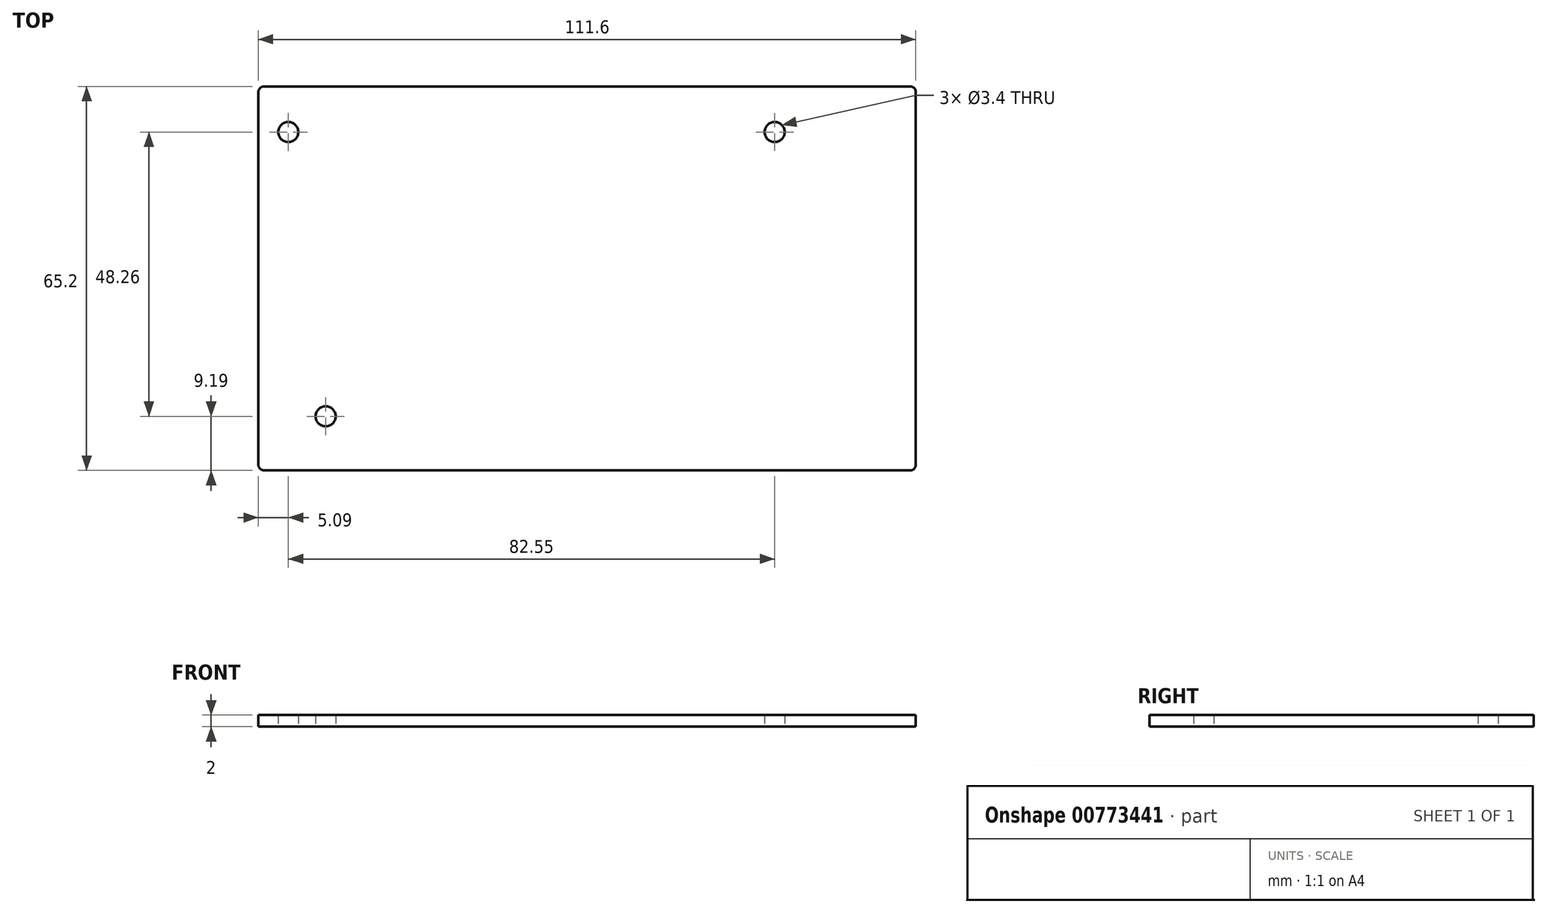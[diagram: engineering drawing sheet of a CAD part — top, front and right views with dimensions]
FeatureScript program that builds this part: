
annotation { "Feature Type Name" : "Feature", "Feature Type Description" : "" }
export const myFeature = defineFeature(function(context is Context, id is Id, definition is map)
    precondition{}
    {
        {
            var Q0;
            Q0=qCreatedBy(makeId("Top.planeOp"),FACE);
            var sketch = newSketch(context, id + "F0", { "sketchPlane" : qUnion([Q0])});
            skLineSegment(sketch, "E0.bottom", {"start": v(54.8, -32.6) * mm, "end": v(-54.8, -32.6) * mm});
            skLineSegment(sketch, "E0.top", {"start": v(54.8, 32.6) * mm, "end": v(-54.8, 32.6) * mm});
            skLineSegment(sketch, "E0.left", {"start": v(55.8, -31.6) * mm, "end": v(55.8, 31.6) * mm});
            skLineSegment(sketch, "E0.right", {"start": v(-55.8, -31.6) * mm, "end": v(-55.8, 31.6) * mm});
            skPoint(sketch, "E0.middle", {"position": v(0, 0) * mm});
            skLineSegment(sketch, "E1", {"start": v(-55.8, -32.6) * mm, "end": v(-55.8, -23.41) * mm, "construction": true});
            skLineSegment(sketch, "E2", {"start": v(-55.8, -32.6) * mm, "end": v(-44.37, -32.6) * mm, "construction": true});
            skLineSegment(sketch, "E3", {"start": v(-55.8, -23.41) * mm, "end": v(-55.8, 24.85) * mm, "construction": true});
            skLineSegment(sketch, "E4", {"start": v(55.8, 32.6) * mm, "end": v(31.84, 32.6) * mm, "construction": true});
            skLineSegment(sketch, "E5", {"start": v(31.84, 32.6) * mm, "end": v(-50.71, 32.6) * mm, "construction": true});
            skPoint(sketch, "E6", {"position": v(-50.71, 24.85) * mm});
            skPoint(sketch, "E7", {"position": v(31.84, 24.85) * mm});
            skPoint(sketch, "E8", {"position": v(-44.37, -23.41) * mm});
            skPoint(sketch, "E9.visualSharp", {"position": v(-55.8, 32.6) * mm});
            skArc(sketch, "E9.filletArc", {"start": v(-54.8, 32.6) * mm, "mid": v(-55.5, 32.3) * mm, "end": v(-55.8, 31.6) * mm});
            skPoint(sketch, "E10.visualSharp", {"position": v(55.8, 32.6) * mm});
            skArc(sketch, "E10.filletArc", {"start": v(55.8, 31.6) * mm, "mid": v(55.5, 32.3) * mm, "end": v(54.8, 32.6) * mm});
            skPoint(sketch, "E11.visualSharp", {"position": v(55.8, -32.6) * mm});
            skArc(sketch, "E11.filletArc", {"start": v(54.8, -32.6) * mm, "mid": v(55.5, -32.3) * mm, "end": v(55.8, -31.6) * mm});
            skPoint(sketch, "E12.visualSharp", {"position": v(-55.8, -32.6) * mm});
            skArc(sketch, "E12.filletArc", {"start": v(-55.8, -31.6) * mm, "mid": v(-55.5, -32.3) * mm, "end": v(-54.8, -32.6) * mm});
            skSolve(sketch);
        }
        {
            var Q0;
            Q0 = qSketchRegion(id + "F0", true);
            extrude(context, id + "F1", {"entities" : qUnion([Q0]), "depth" : 2 * mm, "offsetDistance" : 25 * mm});
        }
        {
            var Q0;
            Q0=sQuery(id+"F0.wireOp",VERTEX,"E6");
            var Q1;
            Q1=sQuery(id+"F0.wireOp",VERTEX,"E8");
            var Q2;
            Q2=sQuery(id+"F0.wireOp",VERTEX,"E7");
            var Q3;
            Q3=makeQuery(id+"F1.opExtrude","SWEPT_BODY",BODY,{"disambiguationData":[OSD([sQuery(id+"F0.wireOp",EDGE,"E0.bottom"),sQuery(id+"F0.wireOp",EDGE,"E0.top"),sQuery(id+"F0.wireOp",EDGE,"E0.left"),sQuery(id+"F0.wireOp",EDGE,"E0.right"),sQuery(id+"F0.wireOp",EDGE,"E9.filletArc"),sQuery(id+"F0.wireOp",EDGE,"E10.filletArc"),sQuery(id+"F0.wireOp",EDGE,"E11.filletArc"),sQuery(id+"F0.wireOp",EDGE,"E12.filletArc")])]});
            hole(context, id + "F2", {"style" : HoleStyle.SIMPLE, "endStyle" : HoleEndStyle.THROUGH, "oppositeDirection" : true, "standardTappedOrClearance" : lookupTablePath({ "fit" : "Normal", "standard" : "ISO", "size" : "M3", "type" : "Clearance" }), "standardBlindInLast" : lookupTablePath({ "fit" : "Normal", "standard" : "ISO", "size" : "M3", "type" : "Clearance" }), "holeDiameter" : 3.4 * mm, "majorDiameter" : 5 * mm, "tappedDepth" : 12 * mm, "tapClearance" : 3, "startFromSketch" : true, "locations" : qUnion([Q0, Q1, Q2]), "scope" : qUnion([Q3])});
        }
    });
